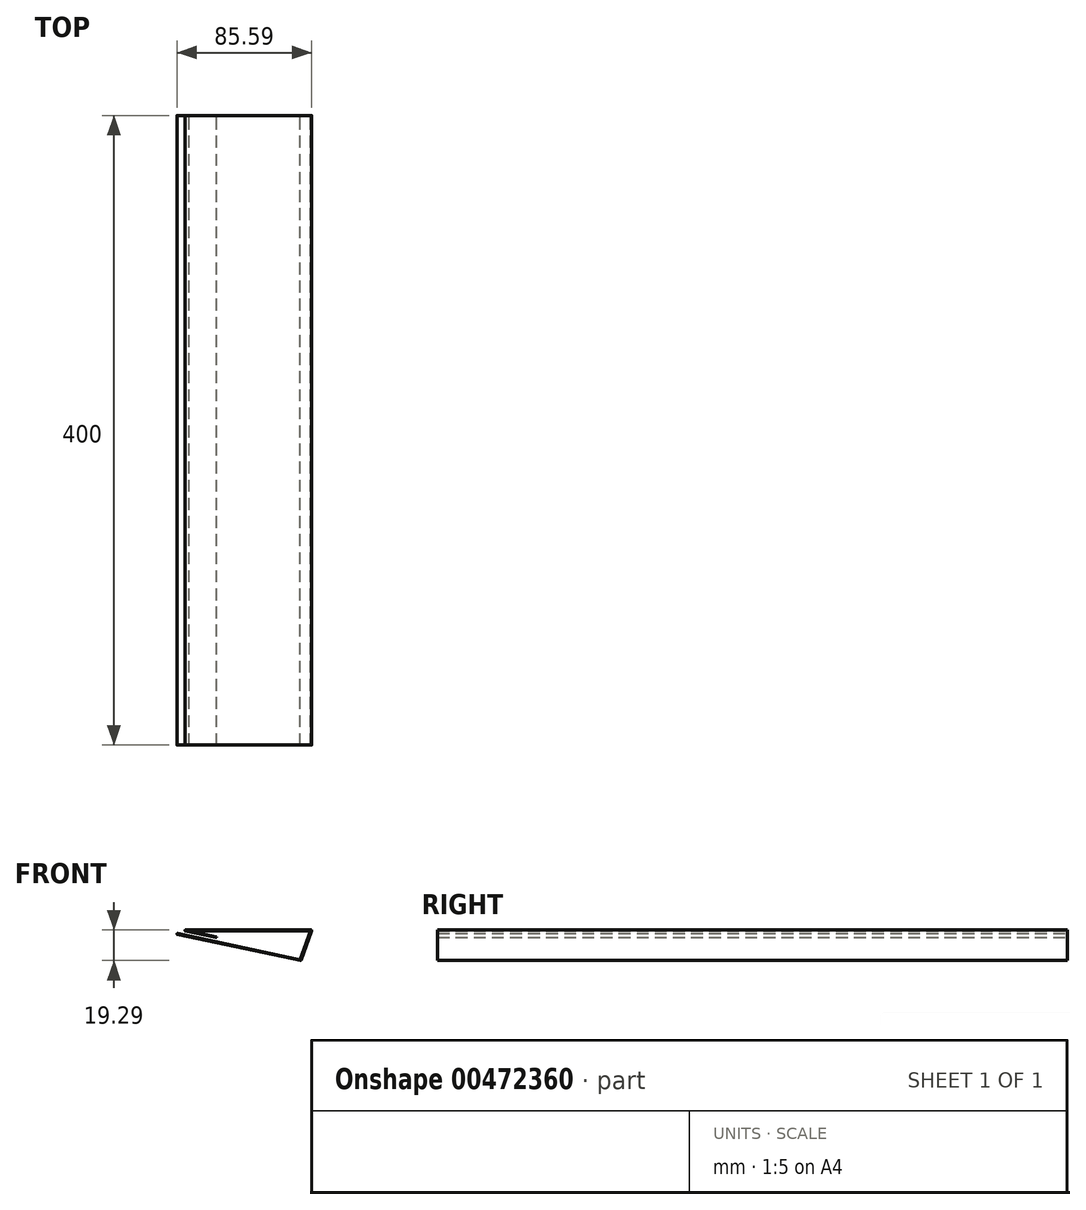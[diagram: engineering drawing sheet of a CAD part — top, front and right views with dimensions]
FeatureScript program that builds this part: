
annotation { "Feature Type Name" : "Feature", "Feature Type Description" : "" }
export const myFeature = defineFeature(function(context is Context, id is Id, definition is map)
    precondition{}
    {
        {
            var Q0;
            Q0=qCreatedBy(makeId("Front.planeOp"),FACE);
            var sketch = newSketch(context, id + "F0", { "sketchPlane" : qUnion([Q0])});
            skLineSegment(sketch, "E0", {"start": v(0, 0) * mm, "end": v(80, 0) * mm});
            skLineSegment(sketch, "E1", {"start": v(80, 0) * mm, "end": v(73.16, -18.8) * mm});
            skLineSegment(sketch, "E2", {"start": v(73.16, -18.8) * mm, "end": v(-5.1, -2.16) * mm});
            skLineSegment(sketch, "E3", {"start": v(-5.1, -2.16) * mm, "end": v(-5.1, 2.84) * mm});
            skLineSegment(sketch, "E4", {"start": v(0, 0) * mm, "end": v(19.56, -4.16) * mm});
            skArc(sketch, "E5.0.startCap", {"start": v(0, -0.25) * mm, "mid": v(-0.25, 0) * mm, "end": v(0, 0.25) * mm});
            skArc(sketch, "E5.0.endCap", {"start": v(80, 0.25) * mm, "mid": v(80.25, 0) * mm, "end": v(80, -0.25) * mm});
            skLineSegment(sketch, "E5.0.left", {"start": v(0, 0.25) * mm, "end": v(80, 0.25) * mm});
            skLineSegment(sketch, "E5.0.right", {"start": v(0, -0.25) * mm, "end": v(80, -0.25) * mm});
            skArc(sketch, "E5.1.startCap", {"start": v(-0.05, -0.24) * mm, "mid": v(-0.24, 0.05) * mm, "end": v(0.05, 0.24) * mm});
            skArc(sketch, "E5.1.endCap", {"start": v(19.61, -3.91) * mm, "mid": v(19.8, -4.21) * mm, "end": v(19.51, -4.4) * mm});
            skLineSegment(sketch, "E5.1.left", {"start": v(0.05, 0.24) * mm, "end": v(19.61, -3.91) * mm});
            skLineSegment(sketch, "E5.1.right", {"start": v(-0.05, -0.24) * mm, "end": v(19.51, -4.4) * mm});
            skArc(sketch, "E5.2.startCap", {"start": v(79.77, 0.09) * mm, "mid": v(80.09, 0.23) * mm, "end": v(80.23, -0.09) * mm});
            skArc(sketch, "E5.2.endCap", {"start": v(73.4, -18.88) * mm, "mid": v(73.07, -19.03) * mm, "end": v(72.92, -18.7) * mm});
            skLineSegment(sketch, "E5.2.left", {"start": v(80.23, -0.09) * mm, "end": v(73.4, -18.88) * mm});
            skLineSegment(sketch, "E5.2.right", {"start": v(79.77, 0.09) * mm, "end": v(72.92, -18.7) * mm});
            skArc(sketch, "E5.3.startCap", {"start": v(73.21, -18.55) * mm, "mid": v(73.4, -18.85) * mm, "end": v(73.1, -19.04) * mm});
            skArc(sketch, "E5.3.endCap", {"start": v(-5.14, -2.4) * mm, "mid": v(-5.34, -2.1) * mm, "end": v(-5.04, -1.92) * mm});
            skLineSegment(sketch, "E5.3.left", {"start": v(73.1, -19.04) * mm, "end": v(-5.14, -2.4) * mm});
            skLineSegment(sketch, "E5.3.right", {"start": v(73.21, -18.55) * mm, "end": v(-5.04, -1.92) * mm});
            skArc(sketch, "E5.4.startCap", {"start": v(-4.84, -2.16) * mm, "mid": v(-5.1, -2.41) * mm, "end": v(-5.34, -2.16) * mm});
            skArc(sketch, "E5.4.endCap", {"start": v(-5.34, 2.84) * mm, "mid": v(-5.1, 3.09) * mm, "end": v(-4.84, 2.84) * mm});
            skLineSegment(sketch, "E5.4.left", {"start": v(-5.34, -2.16) * mm, "end": v(-5.34, 2.84) * mm});
            skLineSegment(sketch, "E5.4.right", {"start": v(-4.84, -2.16) * mm, "end": v(-4.84, 2.84) * mm});
            skSolve(sketch);
        }
        {
            var Q0;
            {var subQ5=sQuery(id+"F0.wireOp",EDGE,"E5.0.left");Q0=makeQuery(id+"F0.imprint","IMPRINT",FACE,{"disambiguationData":[TD([[makeQuery(id+"F0.imprint","IMPRINT",EDGE,{"derivedFrom":subQ5}),-1.0]])]});}
            var Q1;
            {var subQ4=sQuery(id+"F0.wireOp",EDGE,"E5.0.startCap");Q1=makeQuery(id+"F0.imprint","IMPRINT",FACE,{"disambiguationData":[TD([[makeQuery(id+"F0.imprint","IMPRINT",EDGE,{"derivedFrom":subQ4}),1.0]])]});}
            var Q2;
            {var subQ1=sQuery(id+"F0.wireOp",EDGE,"E5.2.endCap");var subQ5=sQuery(id+"F0.wireOp",EDGE,"E2");var subQ6=makeQuery(id+"F0.imprint","INTERSECT",VERTEX,{"derivedFrom":[subQ5,subQ1]});Q2=makeQuery(id+"F0.imprint","IMPRINT",FACE,{"disambiguationData":[TD([[makeQuery(id+"F0.imprint","IMPRINT",EDGE,{"disambiguationData":[TD([[subQ6,-1.0]])],"derivedFrom":subQ5}),-1.0]])]});}
            var Q3;
            {var subQ0=sQuery(id+"F0.wireOp",EDGE,"E5.1.left");var subQ1=sQuery(id+"F0.wireOp",EDGE,"E0");var subQ2=makeQuery(id+"F0.imprint","INTERSECT",VERTEX,{"derivedFrom":[subQ1,subQ0]});Q3=makeQuery(id+"F0.imprint","IMPRINT",FACE,{"disambiguationData":[TD([[makeQuery(id+"F0.imprint","IMPRINT",EDGE,{"disambiguationData":[TD([[subQ2,-1.0]])],"derivedFrom":subQ1}),-1.0]])]});}
            var Q4;
            {var subQ2=sQuery(id+"F0.wireOp",EDGE,"E5.0.endCap");Q4=makeQuery(id+"F0.imprint","IMPRINT",FACE,{"disambiguationData":[TD([[makeQuery(id+"F0.imprint","IMPRINT",EDGE,{"derivedFrom":subQ2}),1.0]])]});}
            var Q5;
            {var subQ3=sQuery(id+"F0.wireOp",EDGE,"E1");var subQ6=sQuery(id+"F0.wireOp",EDGE,"E5.0.right");var subQ9=makeQuery(id+"F0.imprint","INTERSECT",VERTEX,{"derivedFrom":[subQ3,subQ6]});Q5=makeQuery(id+"F0.imprint","IMPRINT",FACE,{"disambiguationData":[TD([[makeQuery(id+"F0.imprint","IMPRINT",EDGE,{"disambiguationData":[TD([[subQ9,-1.0]])],"derivedFrom":subQ3}),-1.0]])]});}
            var Q6;
            {var subQ5=sQuery(id+"F0.wireOp",EDGE,"E5.3.left");Q6=makeQuery(id+"F0.imprint","IMPRINT",FACE,{"disambiguationData":[TD([[makeQuery(id+"F0.imprint","IMPRINT",EDGE,{"derivedFrom":subQ5}),-1.0]])]});}
            var Q7;
            {var subQ0=sQuery(id+"F0.wireOp",EDGE,"E4");var subQ1=sQuery(id+"F0.wireOp",EDGE,"E0");var subQ2=makeQuery(id+"F0.imprint","INTERSECT",VERTEX,{"derivedFrom":[subQ1,subQ0]});Q7=makeQuery(id+"F0.imprint","IMPRINT",FACE,{"disambiguationData":[TD([[makeQuery(id+"F0.imprint","IMPRINT",EDGE,{"disambiguationData":[TD([[subQ2,-1.0]])],"derivedFrom":subQ1}),-1.0]])]});}
            var Q8;
            {var subQ0=sQuery(id+"F0.wireOp",EDGE,"E5.4.endCap");Q8=makeQuery(id+"F0.imprint","IMPRINT",FACE,{"disambiguationData":[TD([[makeQuery(id+"F0.imprint","IMPRINT",EDGE,{"derivedFrom":subQ0}),-1.0]])]});}
            var Q9;
            {var subQ1=sQuery(id+"F0.wireOp",EDGE,"E5.0.startCap");Q9=makeQuery(id+"F0.imprint","IMPRINT",FACE,{"disambiguationData":[TD([[makeQuery(id+"F0.imprint","IMPRINT",EDGE,{"derivedFrom":subQ1}),-1.0]])]});}
            var Q10;
            {var subQ1=sQuery(id+"F0.wireOp",EDGE,"E5.0.endCap");Q10=makeQuery(id+"F0.imprint","IMPRINT",FACE,{"disambiguationData":[TD([[makeQuery(id+"F0.imprint","IMPRINT",EDGE,{"derivedFrom":subQ1}),-1.0]])]});}
            var Q11;
            {var subQ3=sQuery(id+"F0.wireOp",EDGE,"E3");var subQ5=sQuery(id+"F0.wireOp",EDGE,"E2");var subQ6=makeQuery(id+"F0.imprint","INTERSECT",VERTEX,{"derivedFrom":[subQ5,subQ3]});Q11=makeQuery(id+"F0.imprint","IMPRINT",FACE,{"disambiguationData":[TD([[makeQuery(id+"F0.imprint","IMPRINT",EDGE,{"disambiguationData":[TD([[subQ6,1.0]])],"derivedFrom":subQ5}),-1.0]])]});}
            var Q12;
            {var subQ0=sQuery(id+"F0.wireOp",EDGE,"E1");var subQ1=sQuery(id+"F0.wireOp",EDGE,"E0");var subQ2=makeQuery(id+"F0.imprint","INTERSECT",VERTEX,{"derivedFrom":[subQ1,subQ0]});Q12=makeQuery(id+"F0.imprint","IMPRINT",FACE,{"disambiguationData":[TD([[makeQuery(id+"F0.imprint","IMPRINT",EDGE,{"disambiguationData":[TD([[subQ2,1.0]])],"derivedFrom":subQ1}),-1.0]])]});}
            var Q13;
            {var subQ3=sQuery(id+"F0.wireOp",EDGE,"E2");var subQ5=sQuery(id+"F0.wireOp",EDGE,"E1");var subQ6=makeQuery(id+"F0.imprint","INTERSECT",VERTEX,{"derivedFrom":[subQ5,subQ3]});Q13=makeQuery(id+"F0.imprint","IMPRINT",FACE,{"disambiguationData":[TD([[makeQuery(id+"F0.imprint","IMPRINT",EDGE,{"disambiguationData":[TD([[subQ6,1.0]])],"derivedFrom":subQ5}),1.0]])]});}
            var Q14;
            {var subQ5=sQuery(id+"F0.wireOp",EDGE,"E2");var subQ7=sQuery(id+"F0.wireOp",EDGE,"E1");var subQ8=makeQuery(id+"F0.imprint","INTERSECT",VERTEX,{"derivedFrom":[subQ7,subQ5]});Q14=makeQuery(id+"F0.imprint","IMPRINT",FACE,{"disambiguationData":[TD([[makeQuery(id+"F0.imprint","IMPRINT",EDGE,{"disambiguationData":[TD([[subQ8,1.0]])],"derivedFrom":subQ7}),-1.0]])]});}
            var Q15;
            {var subQ2=sQuery(id+"F0.wireOp",EDGE,"E2");var subQ4=sQuery(id+"F0.wireOp",EDGE,"E3");var subQ5=makeQuery(id+"F0.imprint","INTERSECT",VERTEX,{"derivedFrom":[subQ2,subQ4]});Q15=makeQuery(id+"F0.imprint","IMPRINT",FACE,{"disambiguationData":[TD([[makeQuery(id+"F0.imprint","IMPRINT",EDGE,{"disambiguationData":[TD([[subQ5,1.0]])],"derivedFrom":subQ2}),1.0]])]});}
            extrude(context, id + "F1", {"entities" : qUnion([Q0, Q1, Q2, Q3, Q4, Q5, Q6, Q7, Q8, Q9, Q10, Q11, Q12, Q13, Q14, Q15]), "endBound" : BoundingType.SYMMETRIC, "depth" : 400 * mm, "offsetDistance" : 25 * mm});
        }
    });
